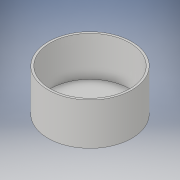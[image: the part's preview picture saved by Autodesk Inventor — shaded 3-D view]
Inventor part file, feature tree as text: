
AUTODESK INVENTOR PART (.ipt)
format: ipt  version: 2019 (Build 230136000, 136)  size: 113,152 bytes
history: native  units: mm
features: sketch x2, other x1, extrude x1, shell x1, hole x1
ambient origin geometry x8: Origin, YZ Plane, XZ Plane, XY Plane, X Axis, Y Axis, Z Axis, Center Point
bodies: Body1 (feature_tree)
feature tree (6):
  other  "Sólido1"
  extrude  "Extrusión1"  Depth=100.0mm TaperAngle=0.0deg
  shell  "Vaciado1"  Thickness=5.0mm
  hole  "Agujero1"  [1 undecoded]
  sketch  "Boceto1"  dims[d0=200.0mm d1=100.0mm d2=0.0mm d3=5.0mm]
  sketch  "Boceto2"  dims[d4=40.241mm d5=6.0mm d6=34.925mm d7=2.0mm d8=14.3117mm d9=8.0mm d10=20.594885mm d11=0.75mm d12=20.594885mm d13=0.0625mm d14=0.75mm d15=0.375mm]
note: 1 required parameter value undecoded (feature->parameter linkage not recoverable at this tier; creation-order binding heuristic only, values carry confidence <= 0.55)
